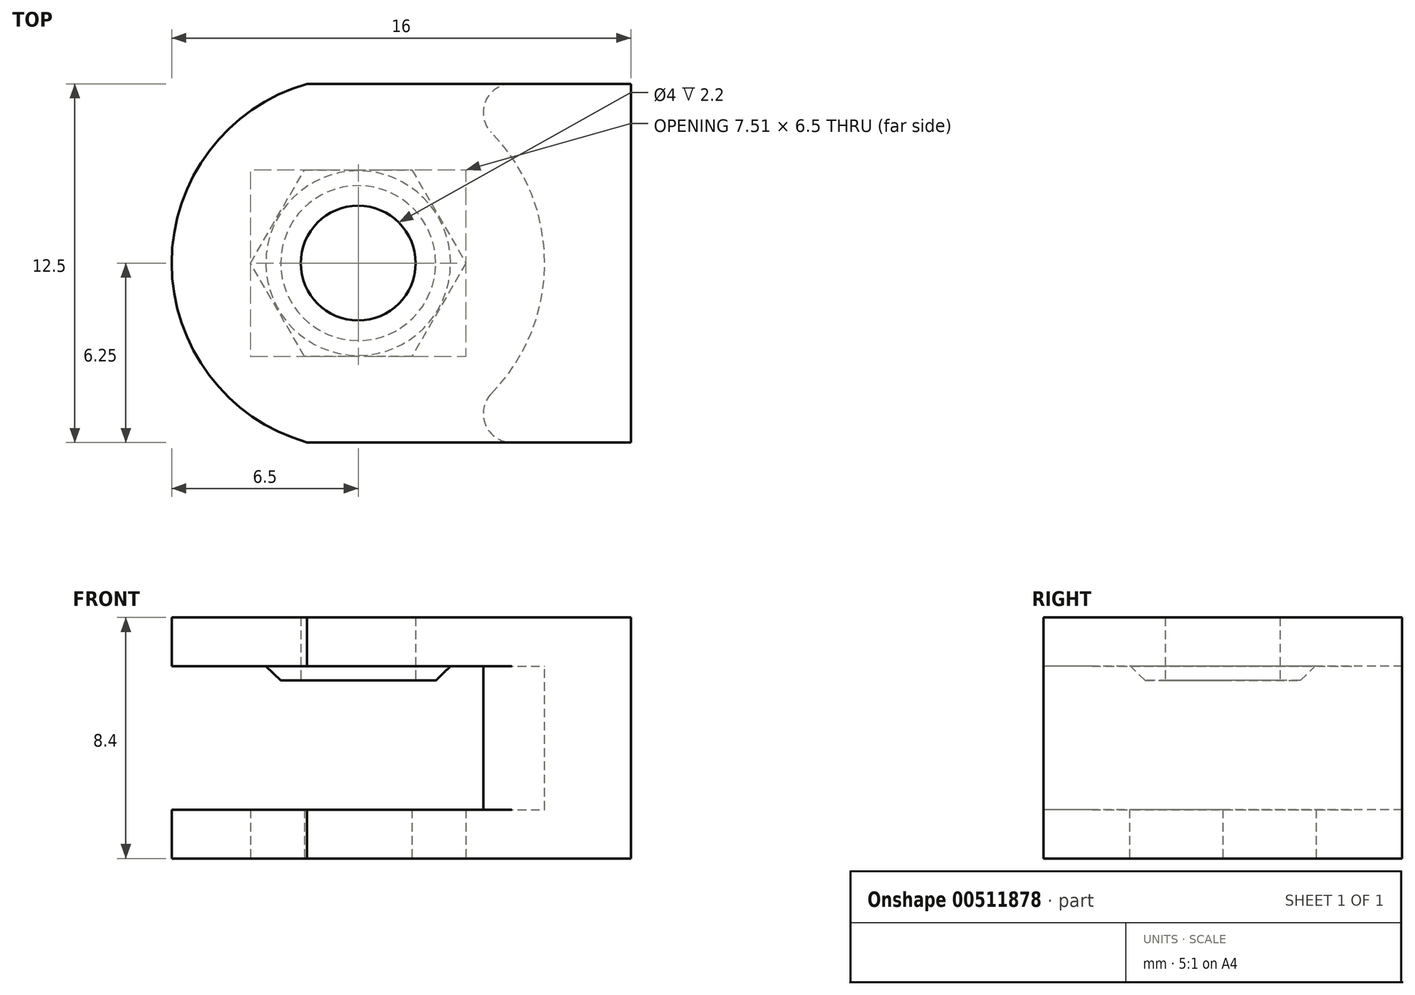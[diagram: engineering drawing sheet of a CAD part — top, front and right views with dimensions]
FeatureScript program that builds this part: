
annotation { "Feature Type Name" : "Feature", "Feature Type Description" : "" }
export const myFeature = defineFeature(function(context is Context, id is Id, definition is map)
    precondition{}
    {
        {
            assignVariable(context, id + "F0", {"name" : "Clearance", "anyValue" : 1 * mm});
        }
        {
            var Q0;
            Q0=qCreatedBy(makeId("Top.planeOp"),FACE);
            var sketch = newSketch(context, id + "F1", { "sketchPlane" : qUnion([Q0])});
            skCircle(sketch, "E0.cCircle", {"center": v(0, 0) * mm, "radius": 3.25 * mm, "construction": true});
            skLineSegment(sketch, "E0.0", {"start": v(-1.88, 3.25) * mm, "end": v(1.88, 3.25) * mm});
            skLineSegment(sketch, "E0.1", {"start": v(1.88, 3.25) * mm, "end": v(3.75, 0) * mm});
            skLineSegment(sketch, "E0.2", {"start": v(3.75, 0) * mm, "end": v(1.88, -3.25) * mm});
            skLineSegment(sketch, "E0.3", {"start": v(1.88, -3.25) * mm, "end": v(-1.88, -3.25) * mm});
            skLineSegment(sketch, "E0.4", {"start": v(-1.88, -3.25) * mm, "end": v(-3.75, 0) * mm});
            skLineSegment(sketch, "E0.5", {"start": v(-3.75, 0) * mm, "end": v(-1.88, 3.25) * mm});
            skPoint(sketch, "E0.0.midPoint", {"position": v(0, 3.25) * mm});
            skLineSegment(sketch, "E1.bottom", {"start": v(-6.75, 6.25) * mm, "end": v(9.5, 6.25) * mm});
            skLineSegment(sketch, "E1.top", {"start": v(-6.75, -6.25) * mm, "end": v(9.5, -6.25) * mm});
            skLineSegment(sketch, "E1.left", {"start": v(-6.75, 6.25) * mm, "end": v(-6.75, -6.25) * mm});
            skLineSegment(sketch, "E1.right", {"start": v(9.5, 6.25) * mm, "end": v(9.5, -6.25) * mm});
            skCircle(sketch, "E2", {"center": v(0, 0) * mm, "radius": 6.5 * mm});
            skCircle(sketch, "E3", {"center": v(0, 0) * mm, "radius": 6 * mm, "construction": true});
            skCircle(sketch, "E4", {"center": v(0, 0) * mm, "radius": 2 * mm});
            skSolve(sketch);
        }
        {
            var Q0;
            Q0=qCreatedBy(makeId("Front.planeOp"),FACE);
            var sketch = newSketch(context, id + "F2", { "sketchPlane" : qUnion([Q0])});
            skLineSegment(sketch, "E5", {"start": v(0, 0) * mm, "end": v(0, 1.7) * mm});
            skLineSegment(sketch, "E6", {"start": v(0, 1.7) * mm, "end": v(0, 6.7) * mm});
            skLineSegment(sketch, "E7", {"start": v(0, 6.7) * mm, "end": v(0, 8.4) * mm});
            skLineSegment(sketch, "E8", {"start": v(6.5, 0) * mm, "end": v(6.5, 8.4) * mm});
            skLineSegment(sketch, "E9", {"start": v(0, 8.4) * mm, "end": v(6.5, 8.4) * mm});
            skLineSegment(sketch, "E10", {"start": v(0, 1.7) * mm, "end": v(6.5, 1.7) * mm});
            skLineSegment(sketch, "E11", {"start": v(0, 6.7) * mm, "end": v(6.5, 6.7) * mm});
            skLineSegment(sketch, "E12", {"start": v(0, 6.2) * mm, "end": v(2.7, 6.2) * mm});
            skLineSegment(sketch, "E13", {"start": v(2.7, 6.2) * mm, "end": v(3.22, 6.7) * mm});
            skLineSegment(sketch, "E14", {"start": v(0, 2.2) * mm, "end": v(6.5, 2.2) * mm, "construction": true});
            skSolve(sketch);
        }
        {
            var Q0;
            {var subQ0=sQuery(id+"F1.wireOp",EDGE,"E1.right");Q0=makeQuery(id+"F1.imprint","IMPRINT",FACE,{"disambiguationData":[TD([[makeQuery(id+"F1.imprint","IMPRINT",EDGE,{"derivedFrom":subQ0}),-1.0]])]});}
            var Q1;
            Q1=makeQuery(id+"F1.imprint","IMPRINT",FACE,{"disambiguationData":[TD([[makeQuery(id+"F1.imprint","IMPRINT",EDGE,{"derivedFrom":sQuery(id+"F1.wireOp",EDGE,"E0.0")}),1.0]])]});
            var Q2;
            Q2=makeQuery(id+"F1.imprint","IMPRINT",FACE,{"disambiguationData":[TD([[makeQuery(id+"F1.imprint","IMPRINT",EDGE,{"derivedFrom":sQuery(id+"F1.wireOp",EDGE,"E0.0")}),-1.0]])]});
            var Q3;
            Q3=sQuery(id+"F2.wireOp",VERTEX,"E9.end");
            extrude(context, id + "F3", {"entities" : qUnion([Q0, Q1, Q2]), "endBound" : BoundingType.UP_TO_VERTEX, "endBoundEntityVertex" : qUnion([Q3]), "depth" : 25 * mm, "offsetDistance" : 25 * mm});
        }
        {
            var Q0;
            {var subQ0=sQuery(id+"F2.wireOp",EDGE,"E10");Q0=makeQuery(id+"F2.imprint","IMPRINT",FACE,{"disambiguationData":[TD([[makeQuery(id+"F2.imprint","IMPRINT",EDGE,{"derivedFrom":subQ0}),1.0]])]});}
            var Q1;
            Q1=sQuery(id+"F2.wireOp",EDGE,"E6");
            revolve(context, id + "F4", {"operationType" : NewBodyOperationType.REMOVE, "entities" : qUnion([Q0]), "axis" : qUnion([Q1]), "revolveType" : RevolveType.FULL, "oppositeDirection" : true});
        }
        {
            var Q0;
            Q0=makeQuery(id+"F3.opExtrude","CAP_FACE",FACE,{"disambiguationData":[OSD([sQuery(id+"F1.wireOp",EDGE,"E1.bottom"),sQuery(id+"F1.wireOp",EDGE,"E1.top"),sQuery(id+"F1.wireOp",EDGE,"E1.right"),sQuery(id+"F1.wireOp",EDGE,"E2"),sQuery(id+"F1.wireOp",EDGE,"E4")])],"isStart":false});
            var sketch = newSketch(context, id + "F5", { "sketchPlane" : qUnion([Q0])});
            skCircle(sketch, "E15", {"center": v(0, 0) * mm, "radius": 2 * mm});
            skSolve(sketch);
        }
        {
            var Q0;
            Q0=makeQuery(id+"F5.imprint","IMPRINT",FACE,{"disambiguationData":[TD([[makeQuery(id+"F5.imprint","IMPRINT",EDGE,{"derivedFrom":sQuery(id+"F5.wireOp",EDGE,"E15")}),1.0]])]});
            extrude(context, id + "F6", {"entities" : qUnion([Q0]), "operationType" : NewBodyOperationType.REMOVE, "oppositeDirection" : true, "depth" : 25 * mm});
        }
        {
            var Q0;
            Q0=makeQuery(id+"F1.imprint","IMPRINT",FACE,{"disambiguationData":[TD([[makeQuery(id+"F1.imprint","IMPRINT",EDGE,{"derivedFrom":sQuery(id+"F1.wireOp",EDGE,"E0.0")}),-1.0]])]});
            var Q1;
            Q1=makeQuery(id+"F4.boolean.opBoolean","COPY",FACE,{"derivedFrom":makeQuery(id+"F4.opRevolve","SWEPT_FACE",FACE,{"disambiguationData":[OSD([sQuery(id+"F2.wireOp",EDGE,"E10")])]})});
            extrude(context, id + "F7", {"entities" : qUnion([Q0]), "operationType" : NewBodyOperationType.REMOVE, "endBound" : BoundingType.UP_TO_SURFACE, "endBoundEntityFace" : qUnion([Q1]), "depth" : 25 * mm});
        }
        {
            var Q0;
            Q0=makeQuery(id+"F4.boolean.opBoolean","INTERSECT",EDGE,{"derivedFrom":[makeQuery(id+"F3.opExtrude","SWEPT_FACE",FACE,{"disambiguationData":[OSD([sQuery(id+"F1.wireOp",EDGE,"E1.bottom")])]}),makeQuery(id+"F4.opRevolve","SWEPT_FACE",FACE,{"disambiguationData":[OSD([sQuery(id+"F2.wireOp",EDGE,"E8")])]})]});
            var Q1;
            Q1=makeQuery(id+"F4.boolean.opBoolean","INTERSECT",EDGE,{"derivedFrom":[makeQuery(id+"F3.opExtrude","SWEPT_FACE",FACE,{"disambiguationData":[OSD([sQuery(id+"F1.wireOp",EDGE,"E1.top")])]}),makeQuery(id+"F4.opRevolve","SWEPT_FACE",FACE,{"disambiguationData":[OSD([sQuery(id+"F2.wireOp",EDGE,"E8")])]})]});
            fillet(context, id + "F8", {"entities" : qUnion([Q0, Q1]), "radius" : getVariable(context, 'Clearance'), "tangentPropagation" : true, "allowEdgeOverflow" : false});
        }
    });
